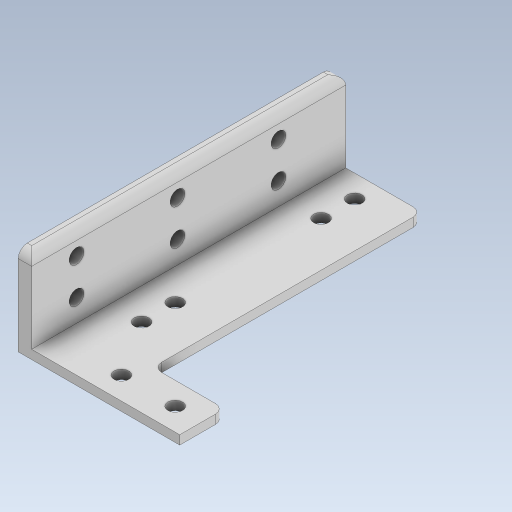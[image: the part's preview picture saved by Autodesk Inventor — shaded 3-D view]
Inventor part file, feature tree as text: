
AUTODESK INVENTOR PART (.ipt)
format: ipt  version: 2023.5 (Build 275446000, 446)  size: 365,056 bytes
history: native  units: mm
features: extrude x3, sketch x2, fillet x1
ambient origin geometry x8: Origin, YZ Plane, XZ Plane, XY Plane, X Axis, Y Axis, Z Axis, Center Point
bodies: Solid1 (feature_tree)
feature tree (6):
  sketch  "Sketch1"  dims[d10=2.0mm d11=0.0mm d12=20.0mm d13=0.0mm]
  extrude  "Extrusion1"  Depth=20.0mm TaperAngle=0.0deg
  extrude  "Extrusion2"  Depth=20.0mm
  extrude  "Extrusion4"  Depth=2.0mm
  fillet  "Fillet1"  Radius=40.0mm
  sketch  "Sketch3"  dims[d22=3.3mm d23=20.0mm d24=3.3mm d25=40.0mm d26=5.0mm d27=3.3mm d28=5.0mm d29=10.0mm d30=3.3mm d31=22.5mm d32=3.3mm d33=8.0mm d34=3.3mm d35=20.0mm d36=0.0mm d37=2.0mm]
